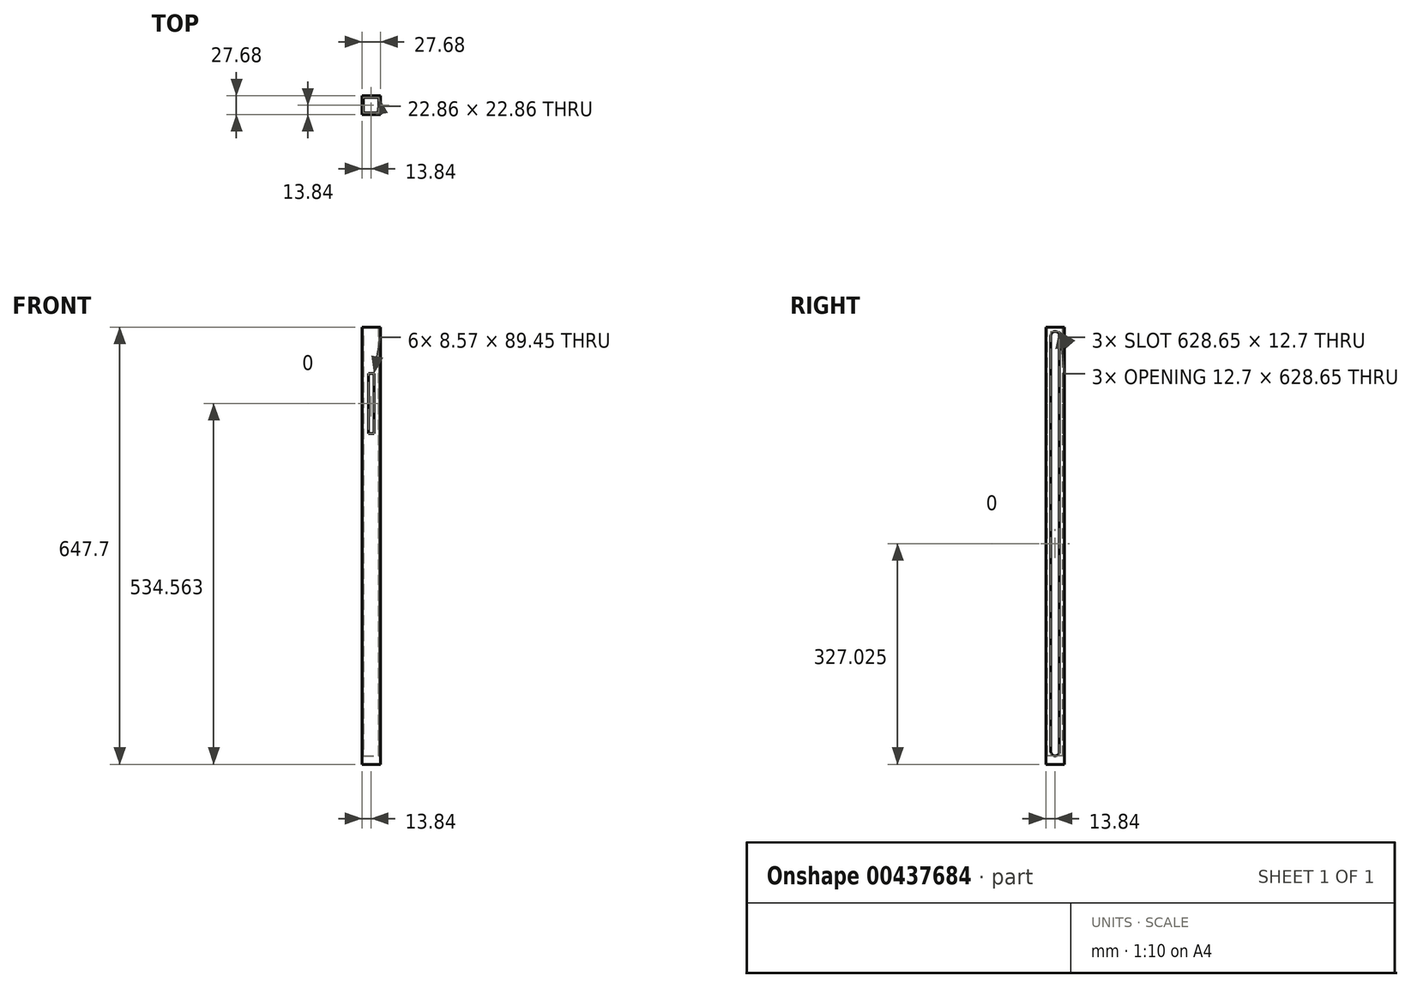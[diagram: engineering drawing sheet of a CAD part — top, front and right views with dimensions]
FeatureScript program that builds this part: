
annotation { "Feature Type Name" : "Feature", "Feature Type Description" : "" }
export const myFeature = defineFeature(function(context is Context, id is Id, definition is map)
    precondition{}
    {
        {
            var Q0;
            Q0=qCreatedBy(makeId("Top.planeOp"),FACE);
            var sketch = newSketch(context, id + "F0", { "sketchPlane" : qUnion([Q0])});
            skLineSegment(sketch, "E0.bottom", {"start": v(-13.84, 13.84) * mm, "end": v(13.84, 13.84) * mm});
            skLineSegment(sketch, "E0.top", {"start": v(-13.84, -13.84) * mm, "end": v(13.84, -13.84) * mm});
            skLineSegment(sketch, "E0.left", {"start": v(-13.84, 13.84) * mm, "end": v(-13.84, -13.84) * mm});
            skLineSegment(sketch, "E0.right", {"start": v(13.84, 13.84) * mm, "end": v(13.84, -13.84) * mm});
            skPoint(sketch, "E0.middle", {"position": v(0, 0) * mm});
            skSolve(sketch);
        }
        {
            var Q0;
            Q0=makeQuery(id+"F0.imprint","IMPRINT",FACE,{"disambiguationData":[TD([[makeQuery(id+"F0.imprint","IMPRINT",EDGE,{"derivedFrom":sQuery(id+"F0.wireOp",EDGE,"E0.bottom")}),-1.0]])]});
            extrude(context, id + "F1", {"entities" : qUnion([Q0]), "depth" : 647.7 * mm});
        }
        {
            var Q0;
            Q0=makeQuery(id+"F1.opExtrude","CAP_FACE",FACE,{"disambiguationData":[OSD([sQuery(id+"F0.wireOp",EDGE,"E0.bottom"),sQuery(id+"F0.wireOp",EDGE,"E0.top"),sQuery(id+"F0.wireOp",EDGE,"E0.left"),sQuery(id+"F0.wireOp",EDGE,"E0.right")])],"isStart":false});
            var sketch = newSketch(context, id + "F2", { "sketchPlane" : qUnion([Q0])});
            skLineSegment(sketch, "E1.bottom", {"start": v(-11.43, 11.43) * mm, "end": v(11.43, 11.43) * mm});
            skLineSegment(sketch, "E1.top", {"start": v(-11.43, -11.43) * mm, "end": v(11.43, -11.43) * mm});
            skLineSegment(sketch, "E1.left", {"start": v(-11.43, 11.43) * mm, "end": v(-11.43, -11.43) * mm});
            skLineSegment(sketch, "E1.right", {"start": v(11.43, 11.43) * mm, "end": v(11.43, -11.43) * mm});
            skPoint(sketch, "E1.middle", {"position": v(0, 0) * mm});
            skSolve(sketch);
        }
        {
            var Q0;
            Q0=makeQuery(id+"F2.imprint","IMPRINT",FACE,{"disambiguationData":[TD([[makeQuery(id+"F2.imprint","IMPRINT",EDGE,{"derivedFrom":sQuery(id+"F2.wireOp",EDGE,"E1.bottom")}),-1.0]])]});
            extrude(context, id + "F3", {"entities" : qUnion([Q0]), "operationType" : NewBodyOperationType.REMOVE, "oppositeDirection" : true, "depth" : 635 * mm});
        }
        {
            var Q0;
            Q0=makeQuery(id+"F1.opExtrude","SWEPT_FACE",FACE,{"disambiguationData":[OSD([sQuery(id+"F0.wireOp",EDGE,"E0.right")])]});
            var sketch = newSketch(context, id + "F4", { "sketchPlane" : qUnion([Q0])});
            skLineSegment(sketch, "E2", {"start": v(0, 647.7) * mm, "end": v(0, 0) * mm});
            skLineSegment(sketch, "E3", {"start": v(-13.84, 323.85) * mm, "end": v(13.84, 323.85) * mm});
            skCircle(sketch, "E4", {"center": v(0, 635) * mm, "radius": 6.35 * mm});
            skCircle(sketch, "E5", {"center": v(0, 19.05) * mm, "radius": 6.35 * mm});
            skLineSegment(sketch, "E6.bottom", {"start": v(-6.35, 19.05) * mm, "end": v(6.35, 19.05) * mm});
            skLineSegment(sketch, "E6.top", {"start": v(-6.35, 635) * mm, "end": v(6.35, 635) * mm});
            skLineSegment(sketch, "E6.left", {"start": v(-6.35, 19.05) * mm, "end": v(-6.35, 635) * mm});
            skLineSegment(sketch, "E6.right", {"start": v(6.35, 19.05) * mm, "end": v(6.35, 635) * mm});
            skSolve(sketch);
        }
        {
            var Q0;
            {var subQ0=sQuery(id+"F4.wireOp",EDGE,"E4");var subQ1=sQuery(id+"F4.wireOp",EDGE,"E2");var subQ2=makeQuery(id+"F4.imprint","INTERSECT",VERTEX,{"disambiguationData":[OD(1.0)],"derivedFrom":[subQ1,subQ0]});Q0=makeQuery(id+"F4.imprint","IMPRINT",FACE,{"disambiguationData":[TD([[makeQuery(id+"F4.imprint","IMPRINT",EDGE,{"disambiguationData":[TD([[subQ2,-1.0]])],"derivedFrom":subQ1}),-1.0]])]});}
            var Q1;
            {var subQ0=sQuery(id+"F4.wireOp",EDGE,"E6.top");var subQ1=sQuery(id+"F4.wireOp",EDGE,"E2");var subQ2=makeQuery(id+"F4.imprint","INTERSECT",VERTEX,{"derivedFrom":[subQ1,subQ0]});Q1=makeQuery(id+"F4.imprint","IMPRINT",FACE,{"disambiguationData":[TD([[makeQuery(id+"F4.imprint","IMPRINT",EDGE,{"disambiguationData":[TD([[subQ2,-1.0]])],"derivedFrom":subQ1}),-1.0]])]});}
            var Q2;
            {var subQ0=sQuery(id+"F4.wireOp",EDGE,"E4");var subQ1=sQuery(id+"F4.wireOp",EDGE,"E2");var subQ2=makeQuery(id+"F4.imprint","INTERSECT",VERTEX,{"disambiguationData":[OD(0.0)],"derivedFrom":[subQ1,subQ0]});Q2=makeQuery(id+"F4.imprint","IMPRINT",FACE,{"disambiguationData":[TD([[makeQuery(id+"F4.imprint","IMPRINT",EDGE,{"disambiguationData":[TD([[subQ2,-1.0]])],"derivedFrom":subQ1}),-1.0]])]});}
            var Q3;
            {var subQ0=sQuery(id+"F4.wireOp",EDGE,"E4");var subQ1=sQuery(id+"F4.wireOp",EDGE,"E2");var subQ2=makeQuery(id+"F4.imprint","INTERSECT",VERTEX,{"disambiguationData":[OD(0.0)],"derivedFrom":[subQ1,subQ0]});Q3=makeQuery(id+"F4.imprint","IMPRINT",FACE,{"disambiguationData":[TD([[makeQuery(id+"F4.imprint","IMPRINT",EDGE,{"disambiguationData":[TD([[subQ2,-1.0]])],"derivedFrom":subQ1}),1.0]])]});}
            var Q4;
            {var subQ0=sQuery(id+"F4.wireOp",EDGE,"E6.top");var subQ1=sQuery(id+"F4.wireOp",EDGE,"E2");var subQ2=makeQuery(id+"F4.imprint","INTERSECT",VERTEX,{"derivedFrom":[subQ1,subQ0]});Q4=makeQuery(id+"F4.imprint","IMPRINT",FACE,{"disambiguationData":[TD([[makeQuery(id+"F4.imprint","IMPRINT",EDGE,{"disambiguationData":[TD([[subQ2,-1.0]])],"derivedFrom":subQ1}),1.0]])]});}
            var Q5;
            {var subQ0=sQuery(id+"F4.wireOp",EDGE,"E4");var subQ1=sQuery(id+"F4.wireOp",EDGE,"E2");var subQ2=makeQuery(id+"F4.imprint","INTERSECT",VERTEX,{"disambiguationData":[OD(1.0)],"derivedFrom":[subQ1,subQ0]});Q5=makeQuery(id+"F4.imprint","IMPRINT",FACE,{"disambiguationData":[TD([[makeQuery(id+"F4.imprint","IMPRINT",EDGE,{"disambiguationData":[TD([[subQ2,-1.0]])],"derivedFrom":subQ1}),1.0]])]});}
            var Q6;
            {var subQ0=sQuery(id+"F4.wireOp",EDGE,"E3");var subQ1=sQuery(id+"F4.wireOp",EDGE,"E2");var subQ2=makeQuery(id+"F4.imprint","INTERSECT",VERTEX,{"derivedFrom":[subQ1,subQ0]});Q6=makeQuery(id+"F4.imprint","IMPRINT",FACE,{"disambiguationData":[TD([[makeQuery(id+"F4.imprint","IMPRINT",EDGE,{"disambiguationData":[TD([[subQ2,-1.0]])],"derivedFrom":subQ1}),-1.0]])]});}
            var Q7;
            {var subQ0=sQuery(id+"F4.wireOp",EDGE,"E3");var subQ1=sQuery(id+"F4.wireOp",EDGE,"E2");var subQ2=makeQuery(id+"F4.imprint","INTERSECT",VERTEX,{"derivedFrom":[subQ1,subQ0]});Q7=makeQuery(id+"F4.imprint","IMPRINT",FACE,{"disambiguationData":[TD([[makeQuery(id+"F4.imprint","IMPRINT",EDGE,{"disambiguationData":[TD([[subQ2,-1.0]])],"derivedFrom":subQ1}),1.0]])]});}
            var Q8;
            {var subQ0=sQuery(id+"F4.wireOp",EDGE,"E6.bottom");var subQ1=sQuery(id+"F4.wireOp",EDGE,"E2");var subQ2=makeQuery(id+"F4.imprint","INTERSECT",VERTEX,{"derivedFrom":[subQ1,subQ0]});Q8=makeQuery(id+"F4.imprint","IMPRINT",FACE,{"disambiguationData":[TD([[makeQuery(id+"F4.imprint","IMPRINT",EDGE,{"disambiguationData":[TD([[subQ2,-1.0]])],"derivedFrom":subQ1}),1.0]])]});}
            var Q9;
            {var subQ0=sQuery(id+"F4.wireOp",EDGE,"E6.bottom");var subQ1=sQuery(id+"F4.wireOp",EDGE,"E2");var subQ2=makeQuery(id+"F4.imprint","INTERSECT",VERTEX,{"derivedFrom":[subQ1,subQ0]});Q9=makeQuery(id+"F4.imprint","IMPRINT",FACE,{"disambiguationData":[TD([[makeQuery(id+"F4.imprint","IMPRINT",EDGE,{"disambiguationData":[TD([[subQ2,-1.0]])],"derivedFrom":subQ1}),-1.0]])]});}
            var Q10;
            {var subQ0=sQuery(id+"F4.wireOp",EDGE,"E5");var subQ1=sQuery(id+"F4.wireOp",EDGE,"E2");var subQ2=makeQuery(id+"F4.imprint","INTERSECT",VERTEX,{"disambiguationData":[OD(0.0)],"derivedFrom":[subQ1,subQ0]});Q10=makeQuery(id+"F4.imprint","IMPRINT",FACE,{"disambiguationData":[TD([[makeQuery(id+"F4.imprint","IMPRINT",EDGE,{"disambiguationData":[TD([[subQ2,-1.0]])],"derivedFrom":subQ1}),-1.0]])]});}
            var Q11;
            {var subQ0=sQuery(id+"F4.wireOp",EDGE,"E5");var subQ1=sQuery(id+"F4.wireOp",EDGE,"E2");var subQ2=makeQuery(id+"F4.imprint","INTERSECT",VERTEX,{"disambiguationData":[OD(0.0)],"derivedFrom":[subQ1,subQ0]});Q11=makeQuery(id+"F4.imprint","IMPRINT",FACE,{"disambiguationData":[TD([[makeQuery(id+"F4.imprint","IMPRINT",EDGE,{"disambiguationData":[TD([[subQ2,-1.0]])],"derivedFrom":subQ1}),1.0]])]});}
            extrude(context, id + "F5", {"entities" : qUnion([Q0, Q1, Q2, Q3, Q4, Q5, Q6, Q7, Q8, Q9, Q10, Q11]), "operationType" : NewBodyOperationType.REMOVE, "oppositeDirection" : true, "depth" : 56.13 * mm});
        }
        {
            var Q0;
            Q0=makeQuery(id+"F1.opExtrude","SWEPT_FACE",FACE,{"disambiguationData":[OSD([sQuery(id+"F0.wireOp",EDGE,"E0.top")])]});
            var sketch = newSketch(context, id + "F6", { "sketchPlane" : qUnion([Q0])});
            skLineSegment(sketch, "E7.bottom", {"start": v(4.28, 489.84) * mm, "end": v(-4.28, 489.84) * mm});
            skLineSegment(sketch, "E7.top", {"start": v(4.28, 805.56) * mm, "end": v(-4.28, 805.56) * mm});
            skLineSegment(sketch, "E7.left", {"start": v(4.28, 489.84) * mm, "end": v(4.28, 805.56) * mm});
            skLineSegment(sketch, "E7.right", {"start": v(-4.28, 489.84) * mm, "end": v(-4.28, 805.56) * mm});
            skPoint(sketch, "E7.middle", {"position": v(0, 647.7) * mm});
            skLineSegment(sketch, "E8", {"start": v(-4.28, 579.29) * mm, "end": v(4.28, 579.29) * mm});
            skSolve(sketch);
        }
        {
            var Q0;
            {var subQ0=sQuery(id+"F6.wireOp",EDGE,"E7.bottom");Q0=makeQuery(id+"F6.imprint","IMPRINT",FACE,{"disambiguationData":[TD([[makeQuery(id+"F6.imprint","IMPRINT",EDGE,{"derivedFrom":subQ0}),-1.0]])]});}
            extrude(context, id + "F7", {"entities" : qUnion([Q0]), "operationType" : NewBodyOperationType.REMOVE, "oppositeDirection" : true, "depth" : 68.33 * mm});
        }
    });
